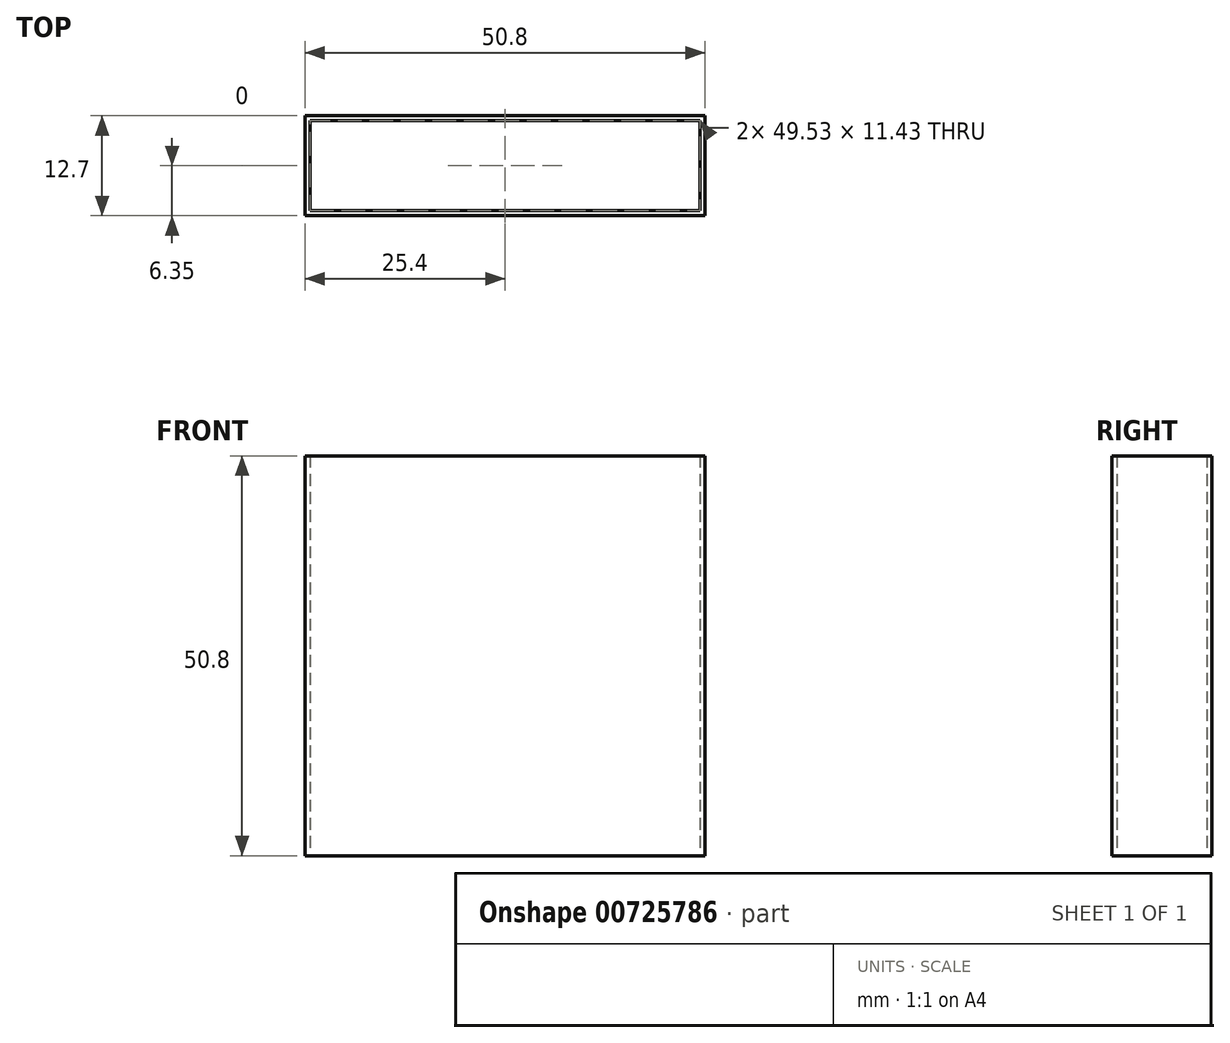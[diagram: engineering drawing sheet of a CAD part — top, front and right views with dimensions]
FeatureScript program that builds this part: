
annotation { "Feature Type Name" : "Feature", "Feature Type Description" : "" }
export const myFeature = defineFeature(function(context is Context, id is Id, definition is map)
    precondition{}
    {
        {
            var Q0;
            Q0=qCreatedBy(makeId("Top.planeOp"),FACE);
            var sketch = newSketch(context, id + "F0", { "sketchPlane" : qUnion([Q0])});
            skLineSegment(sketch, "E0.bottom", {"start": v(-25.4, -6.35) * mm, "end": v(25.4, -6.35) * mm});
            skLineSegment(sketch, "E0.top", {"start": v(-25.4, 6.35) * mm, "end": v(25.4, 6.35) * mm});
            skLineSegment(sketch, "E0.left", {"start": v(-25.4, -6.35) * mm, "end": v(-25.4, 6.35) * mm});
            skLineSegment(sketch, "E0.right", {"start": v(25.4, -6.35) * mm, "end": v(25.4, 6.35) * mm});
            skPoint(sketch, "E0.middle", {"position": v(0, 0) * mm});
            skLineSegment(sketch, "E1.bottom", {"start": v(-24.77, -5.72) * mm, "end": v(24.77, -5.72) * mm});
            skLineSegment(sketch, "E1.top", {"start": v(-24.77, 5.72) * mm, "end": v(24.77, 5.72) * mm});
            skLineSegment(sketch, "E1.left", {"start": v(-24.77, -5.72) * mm, "end": v(-24.77, 5.72) * mm});
            skLineSegment(sketch, "E1.right", {"start": v(24.77, -5.72) * mm, "end": v(24.77, 5.71) * mm});
            skSolve(sketch);
        }
        {
            var Q0;
            Q0=makeQuery(id+"F0.imprint","IMPRINT",FACE,{"disambiguationData":[TD([[makeQuery(id+"F0.imprint","IMPRINT",EDGE,{"derivedFrom":sQuery(id+"F0.wireOp",EDGE,"E0.bottom")}),1.0]])]});
            extrude(context, id + "F1", {"entities" : qUnion([Q0]), "depth" : 50.8 * mm, "offsetDistance" : 25.4 * mm});
        }
    });
